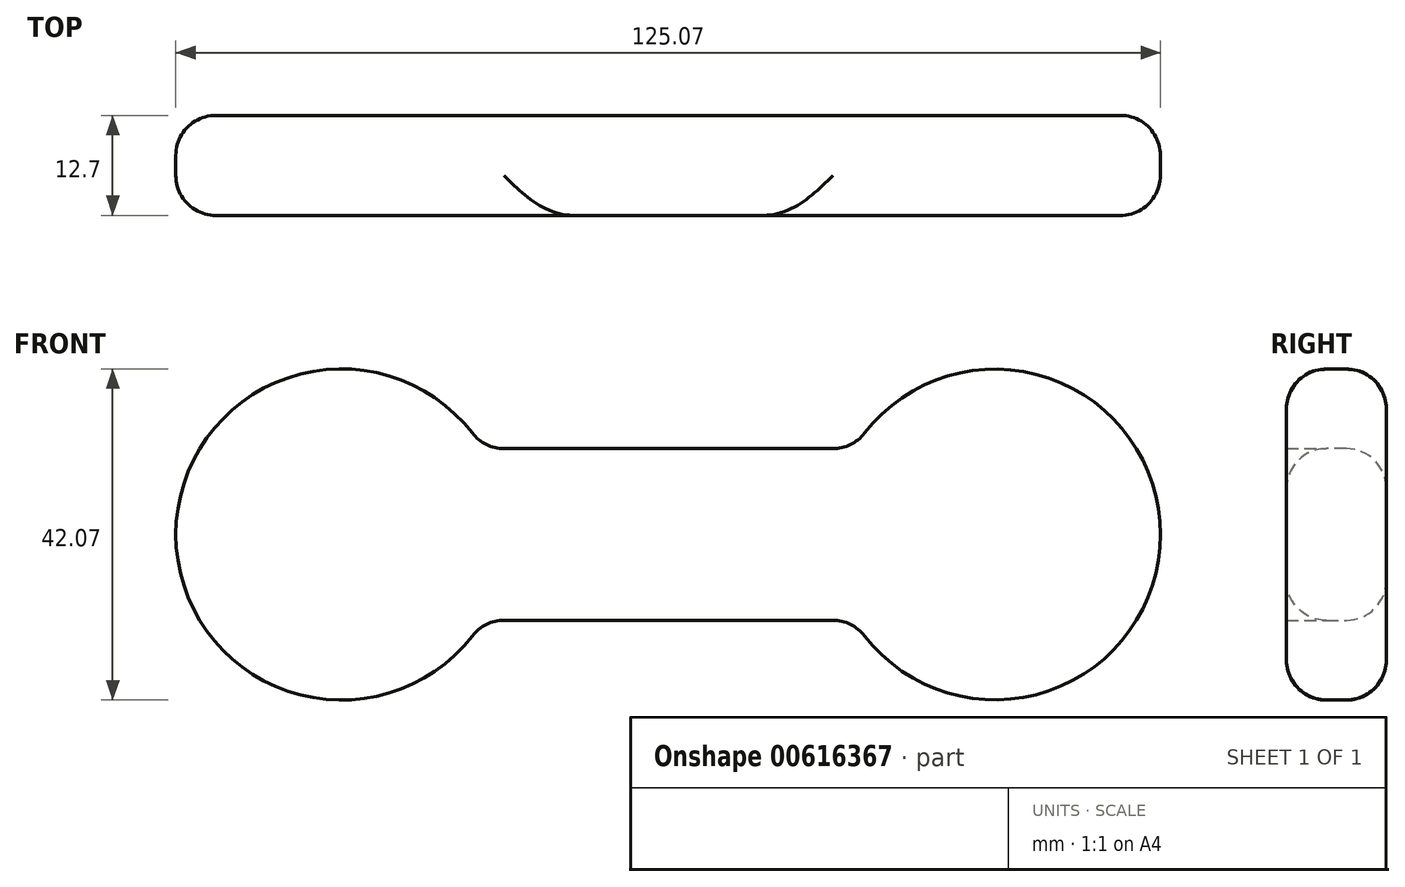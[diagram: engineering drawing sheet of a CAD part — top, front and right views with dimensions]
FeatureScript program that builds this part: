
annotation { "Feature Type Name" : "Feature", "Feature Type Description" : "" }
export const myFeature = defineFeature(function(context is Context, id is Id, definition is map)
    precondition{}
    {
        {
            var Q0;
            Q0=qCreatedBy(makeId("Front.planeOp"),FACE);
            var sketch = newSketch(context, id + "F0", { "sketchPlane" : qUnion([Q0])});
            skLineSegment(sketch, "E0.bottom", {"start": v(42.92, -19.24) * mm, "end": v(-28.54, -19.24) * mm});
            skLineSegment(sketch, "E0.top", {"start": v(42.92, -41.04) * mm, "end": v(-28.54, -41.04) * mm});
            skLineSegment(sketch, "E0.left", {"start": v(42.92, -19.24) * mm, "end": v(42.92, -41.04) * mm});
            skLineSegment(sketch, "E0.right", {"start": v(-28.54, -19.24) * mm, "end": v(-28.54, -41.04) * mm});
            skCircle(sketch, "E1", {"center": v(-33.64, -30.14) * mm, "radius": 21.03 * mm});
            skPoint(sketch, "E1.centerSnap0", {"position": v(-28.54, -30.14) * mm});
            skCircle(sketch, "E2", {"center": v(49.39, -30.14) * mm, "radius": 21 * mm});
            skSolve(sketch);
        }
        {
            var Q0;
            {var subQ0=sQuery(id+"F0.wireOp",EDGE,"E0.right");Q0=makeQuery(id+"F0.imprint","IMPRINT",FACE,{"disambiguationData":[TD([[makeQuery(id+"F0.imprint","IMPRINT",EDGE,{"derivedFrom":subQ0}),-1.0]])]});}
            var Q1;
            {var subQ0=sQuery(id+"F0.wireOp",EDGE,"E0.left");Q1=makeQuery(id+"F0.imprint","IMPRINT",FACE,{"disambiguationData":[TD([[makeQuery(id+"F0.imprint","IMPRINT",EDGE,{"derivedFrom":subQ0}),-1.0]])]});}
            var Q2;
            {var subQ0=sQuery(id+"F0.wireOp",EDGE,"E2");var subQ1=sQuery(id+"F0.wireOp",EDGE,"E0.bottom");var subQ2=makeQuery(id+"F0.imprint","INTERSECT",VERTEX,{"derivedFrom":[subQ1,subQ0]});Q2=makeQuery(id+"F0.imprint","IMPRINT",FACE,{"disambiguationData":[TD([[makeQuery(id+"F0.imprint","IMPRINT",EDGE,{"disambiguationData":[TD([[subQ2,-1.0]])],"derivedFrom":subQ1}),1.0]])]});}
            var Q3;
            {var subQ0=sQuery(id+"F0.wireOp",EDGE,"E0.right");Q3=makeQuery(id+"F0.imprint","IMPRINT",FACE,{"disambiguationData":[TD([[makeQuery(id+"F0.imprint","IMPRINT",EDGE,{"derivedFrom":subQ0}),1.0]])]});}
            var Q4;
            {var subQ0=sQuery(id+"F0.wireOp",EDGE,"E0.left");Q4=makeQuery(id+"F0.imprint","IMPRINT",FACE,{"disambiguationData":[TD([[makeQuery(id+"F0.imprint","IMPRINT",EDGE,{"derivedFrom":subQ0}),1.0]])]});}
            extrude(context, id + "F1", {"entities" : qUnion([Q0, Q1, Q2, Q3, Q4]), "depth" : 12.7 * mm, "offsetDistance" : 25.4 * mm});
        }
        {
            var Q0;
            Q0=makeQuery(id+"F1.opExtrude","CAP_EDGE",EDGE,{"disambiguationData":[OSD([sQuery(id+"F0.wireOp",EDGE,"E1")])],"isStart":true});
            var Q1;
            Q1=makeQuery(id+"F1.opExtrude","SWEPT_FACE",FACE,{"disambiguationData":[OSD([sQuery(id+"F0.wireOp",EDGE,"E1")])]});
            var Q2;
            Q2=makeQuery(id+"F1.opExtrude","CAP_FACE",FACE,{"disambiguationData":[OSD([sQuery(id+"F0.wireOp",EDGE,"E0.bottom"),sQuery(id+"F0.wireOp",EDGE,"E0.top"),sQuery(id+"F0.wireOp",EDGE,"E1"),sQuery(id+"F0.wireOp",EDGE,"E2")])],"isStart":true});
            var Q3;
            Q3=makeQuery(id+"F1.opExtrude","SWEPT_FACE",FACE,{"disambiguationData":[OSD([sQuery(id+"F0.wireOp",EDGE,"E2")])]});
            fillet(context, id + "F2", {"entities" : qUnion([Q0, Q1, Q2, Q3]), "radius" : 5.08 * mm, "tangentPropagation" : true, "allowEdgeOverflow" : false});
        }
    });
